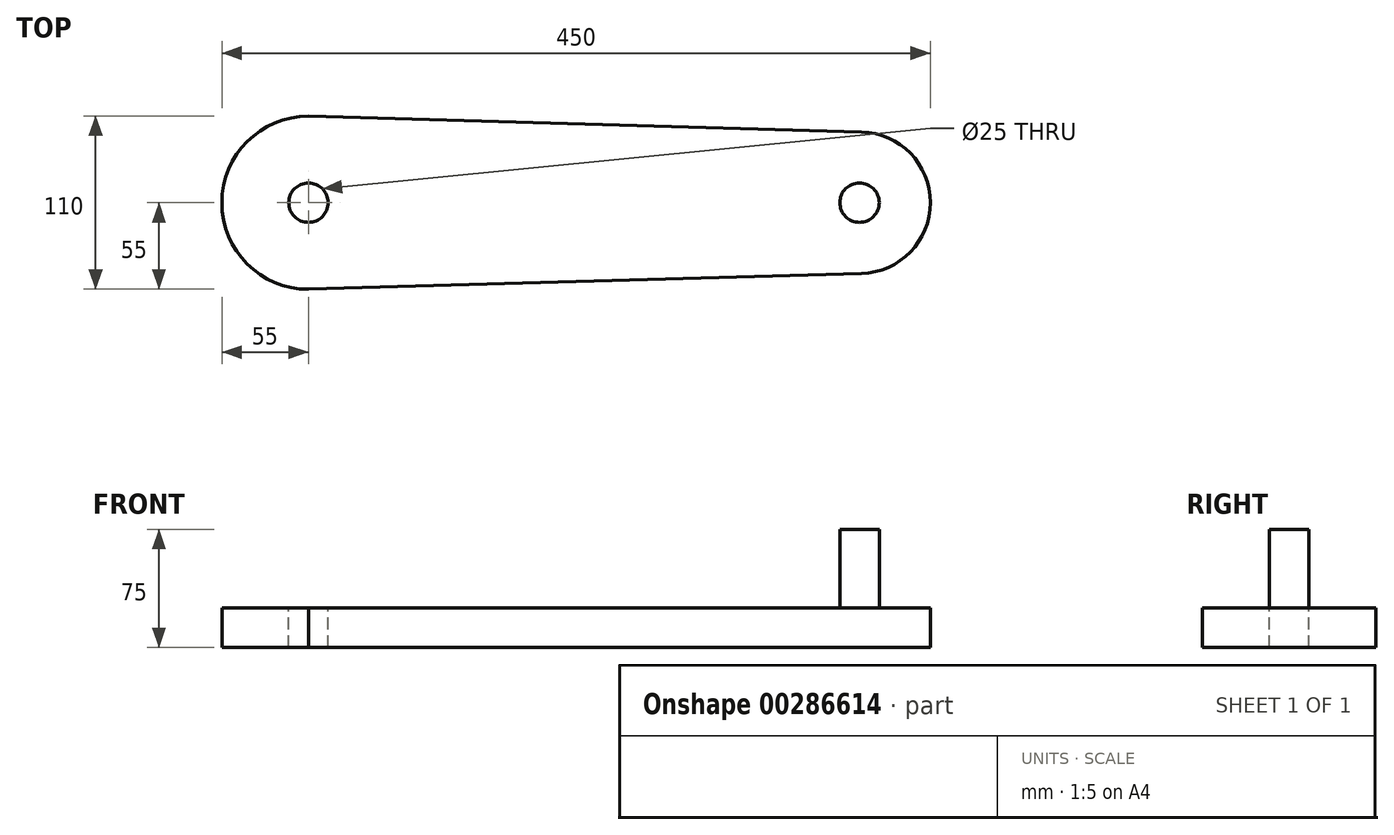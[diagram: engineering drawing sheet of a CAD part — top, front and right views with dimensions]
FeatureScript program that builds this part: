
annotation { "Feature Type Name" : "Feature", "Feature Type Description" : "" }
export const myFeature = defineFeature(function(context is Context, id is Id, definition is map)
    precondition{}
    {
        {
            var Q0;
            Q0=qCreatedBy(makeId("Top.planeOp"),FACE);
            var sketch = newSketch(context, id + "F0", { "sketchPlane" : qUnion([Q0])});
            skArc(sketch, "E0", {"start": v(3.13, 54.91) * mm, "mid": v(-55, 0) * mm, "end": v(3.13, -54.91) * mm});
            skArc(sketch, "E1", {"start": v(351.28, -44.98) * mm, "mid": v(395, 0) * mm, "end": v(351.28, 44.98) * mm});
            skLineSegment(sketch, "E2", {"start": v(0, 55) * mm, "end": v(351.28, 44.98) * mm});
            skLineSegment(sketch, "E3", {"start": v(0, -55) * mm, "end": v(351.28, -44.98) * mm});
            skSolve(sketch);
        }
        {
            var Q0;
            {var subQ3=sQuery(id+"F0.wireOp",EDGE,"E1");Q0=makeQuery(id+"F0.imprint","IMPRINT",FACE,{"disambiguationData":[TD([[makeQuery(id+"F0.imprint","IMPRINT",EDGE,{"derivedFrom":subQ3}),1.0]])]});}
            extrude(context, id + "F1", {"entities" : qUnion([Q0]), "depth" : 25 * mm});
        }
        {
            var Q0;
            Q0=makeQuery(id+"F1.opExtrude","CAP_FACE",FACE,{"disambiguationData":[OSD([sQuery(id+"F0.wireOp",EDGE,"E0"),sQuery(id+"F0.wireOp",EDGE,"E1"),sQuery(id+"F0.wireOp",EDGE,"E2"),sQuery(id+"F0.wireOp",EDGE,"E3")])],"isStart":false});
            var sketch = newSketch(context, id + "F2", { "sketchPlane" : qUnion([Q0])});
            skCircle(sketch, "E4", {"center": v(0, 0) * mm, "radius": 12.5 * mm});
            skSolve(sketch);
        }
        {
            var Q0;
            Q0=makeQuery(id+"F2.imprint","IMPRINT",FACE,{"disambiguationData":[TD([[makeQuery(id+"F2.imprint","IMPRINT",EDGE,{"derivedFrom":sQuery(id+"F2.wireOp",EDGE,"E4")}),1.0]])]});
            extrude(context, id + "F3", {"entities" : qUnion([Q0]), "operationType" : NewBodyOperationType.REMOVE, "endBound" : BoundingType.THROUGH_ALL, "oppositeDirection" : true, "depth" : 25 * mm});
        }
        {
            var Q0;
            Q0=makeQuery(id+"F1.opExtrude","CAP_FACE",FACE,{"disambiguationData":[OSD([sQuery(id+"F0.wireOp",EDGE,"E0"),sQuery(id+"F0.wireOp",EDGE,"E1"),sQuery(id+"F0.wireOp",EDGE,"E2"),sQuery(id+"F0.wireOp",EDGE,"E3")])],"isStart":false});
            var sketch = newSketch(context, id + "F4", { "sketchPlane" : qUnion([Q0])});
            skCircle(sketch, "E5", {"center": v(350, 0) * mm, "radius": 12.5 * mm});
            skSolve(sketch);
        }
        {
            var Q0;
            Q0=makeQuery(id+"F4.imprint","IMPRINT",FACE,{"disambiguationData":[TD([[makeQuery(id+"F4.imprint","IMPRINT",EDGE,{"derivedFrom":sQuery(id+"F4.wireOp",EDGE,"E5")}),1.0]])]});
            extrude(context, id + "F5", {"entities" : qUnion([Q0]), "operationType" : NewBodyOperationType.ADD, "depth" : 50 * mm});
        }
    });
